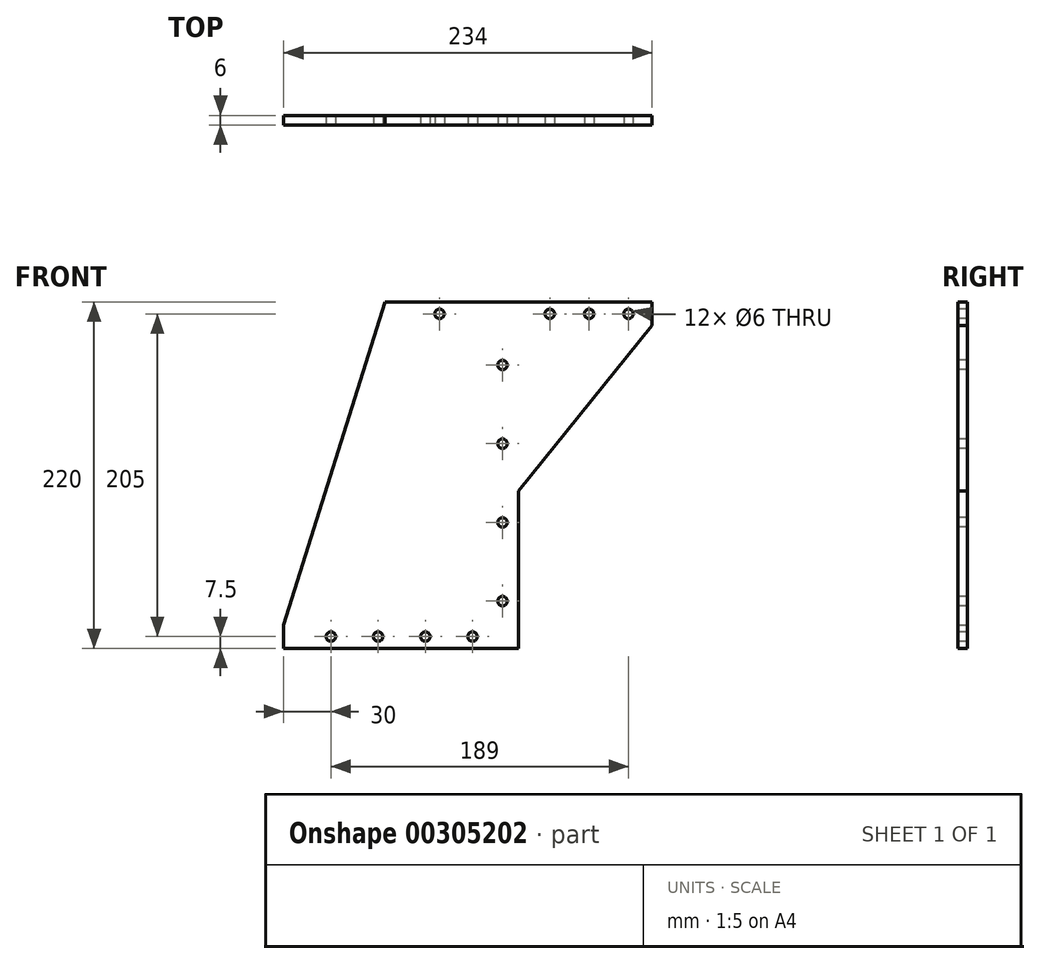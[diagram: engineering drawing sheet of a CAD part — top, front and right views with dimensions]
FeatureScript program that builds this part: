
annotation { "Feature Type Name" : "Feature", "Feature Type Description" : "" }
export const myFeature = defineFeature(function(context is Context, id is Id, definition is map)
    precondition{}
    {
        {
            var Q0;
            Q0=qCreatedBy(makeId("Front.planeOp"),FACE);
            var sketch = newSketch(context, id + "F0", { "sketchPlane" : qUnion([Q0])});
            skLineSegment(sketch, "E0", {"start": v(0, -12.5) * mm, "end": v(100, -12.5) * mm});
            skLineSegment(sketch, "E1", {"start": v(100, -12.5) * mm, "end": v(100, 87.5) * mm});
            skLineSegment(sketch, "E2", {"start": v(130, 207.5) * mm, "end": v(34.41, 207.5) * mm});
            skLineSegment(sketch, "E3", {"start": v(34.41, 207.5) * mm, "end": v(15.27, 207.5) * mm});
            skLineSegment(sketch, "E4", {"start": v(0, -12.5) * mm, "end": v(-49, -12.5) * mm});
            skLineSegment(sketch, "E5", {"start": v(-49, -12.5) * mm, "end": v(-49, 2.5) * mm});
            skLineSegment(sketch, "E6", {"start": v(-49, 2.5) * mm, "end": v(15.27, 207.5) * mm});
            skLineSegment(sketch, "E7", {"start": v(130, 207.5) * mm, "end": v(185, 207.5) * mm});
            skLineSegment(sketch, "E8", {"start": v(185, 207.5) * mm, "end": v(185, 192.5) * mm});
            skLineSegment(sketch, "E9", {"start": v(100, 87.5) * mm, "end": v(185, 192.5) * mm});
            skSolve(sketch);
        }
        {
            var Q0;
            Q0 = qSketchRegion(id + "F0", true);
            extrude(context, id + "F1", {"entities" : qUnion([Q0]), "depth" : 6 * mm});
        }
        {
            var Q0;
            Q0=makeQuery(id+"F1.opExtrude","CAP_FACE",FACE,{"disambiguationData":[OSD([sQuery(id+"F0.wireOp",EDGE,"E0"),sQuery(id+"F0.wireOp",EDGE,"E1"),sQuery(id+"F0.wireOp",EDGE,"E2"),sQuery(id+"F0.wireOp",EDGE,"E3"),sQuery(id+"F0.wireOp",EDGE,"E4"),sQuery(id+"F0.wireOp",EDGE,"E5"),sQuery(id+"F0.wireOp",EDGE,"E6"),sQuery(id+"F0.wireOp",EDGE,"E7"),sQuery(id+"F0.wireOp",EDGE,"E8"),sQuery(id+"F0.wireOp",EDGE,"E9")])],"isStart":false});
            var sketch = newSketch(context, id + "F2", { "sketchPlane" : qUnion([Q0])});
            skPoint(sketch, "E10", {"position": v(170, 200) * mm});
            skPoint(sketch, "E11", {"position": v(145, 200) * mm});
            skPoint(sketch, "E12", {"position": v(120, 200) * mm});
            skPoint(sketch, "E13", {"position": v(90, 167.5) * mm});
            skPoint(sketch, "E14", {"position": v(90, 117.5) * mm});
            skPoint(sketch, "E15", {"position": v(90, 67.5) * mm});
            skPoint(sketch, "E16", {"position": v(90, 17.5) * mm});
            skPoint(sketch, "E17", {"position": v(-19, -5) * mm});
            skPoint(sketch, "E18", {"position": v(11, -5) * mm});
            skPoint(sketch, "E19", {"position": v(41, -5) * mm});
            skPoint(sketch, "E20", {"position": v(71, -5) * mm});
            skPoint(sketch, "E21", {"position": v(50, 200) * mm});
            skSolve(sketch);
        }
        {
            var Q0;
            Q0=sQuery(id+"F2.wireOp",VERTEX,"E12");
            var Q1;
            Q1=sQuery(id+"F2.wireOp",VERTEX,"E11");
            var Q2;
            Q2=sQuery(id+"F2.wireOp",VERTEX,"E10");
            var Q3;
            Q3=sQuery(id+"F2.wireOp",VERTEX,"E13");
            var Q4;
            Q4=sQuery(id+"F2.wireOp",VERTEX,"E14");
            var Q5;
            Q5=sQuery(id+"F2.wireOp",VERTEX,"E15");
            var Q6;
            Q6=sQuery(id+"F2.wireOp",VERTEX,"E16");
            var Q7;
            Q7=sQuery(id+"F2.wireOp",VERTEX,"E19");
            var Q8;
            Q8=sQuery(id+"F2.wireOp",VERTEX,"E18");
            var Q9;
            Q9=sQuery(id+"F2.wireOp",VERTEX,"E17");
            var Q10;
            Q10=sQuery(id+"F2.wireOp",VERTEX,"E20");
            var Q11;
            Q11=sQuery(id+"F2.wireOp",VERTEX,"E21");
            var Q12;
            Q12=makeQuery(id+"F1.opExtrude","SWEPT_BODY",BODY,{"disambiguationData":[OSD([sQuery(id+"F0.wireOp",EDGE,"E0"),sQuery(id+"F0.wireOp",EDGE,"E1"),sQuery(id+"F0.wireOp",EDGE,"E2"),sQuery(id+"F0.wireOp",EDGE,"E3"),sQuery(id+"F0.wireOp",EDGE,"E4"),sQuery(id+"F0.wireOp",EDGE,"E5"),sQuery(id+"F0.wireOp",EDGE,"E6"),sQuery(id+"F0.wireOp",EDGE,"E7"),sQuery(id+"F0.wireOp",EDGE,"E8"),sQuery(id+"F0.wireOp",EDGE,"E9")])]});
            hole(context, id + "F3", {"style" : HoleStyle.SIMPLE, "endStyle" : HoleEndStyle.THROUGH, "holeDiameter" : 6 * mm, "tappedDepth" : 12.6 * mm, "tapClearance" : 3, "startFromSketch" : true, "locations" : qUnion([Q0, Q1, Q2, Q3, Q4, Q5, Q6, Q7, Q8, Q9, Q10, Q11]), "scope" : qUnion([Q12])});
        }
    });
